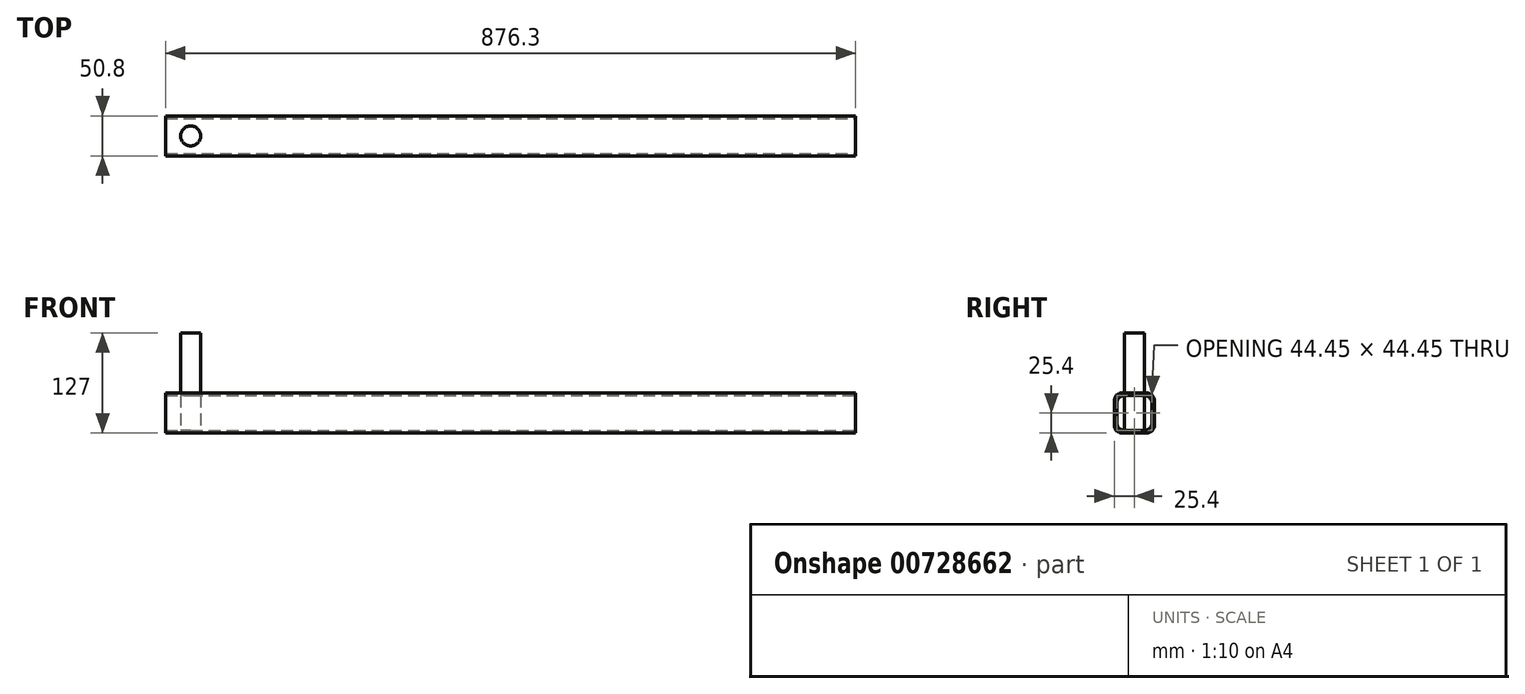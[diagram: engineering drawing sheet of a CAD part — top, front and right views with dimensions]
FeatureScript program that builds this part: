
annotation { "Feature Type Name" : "Feature", "Feature Type Description" : "" }
export const myFeature = defineFeature(function(context is Context, id is Id, definition is map)
    precondition{}
    {
        {
            var Q0;
            Q0=qCreatedBy(makeId("Right.planeOp"),FACE);
            var sketch = newSketch(context, id + "F0", { "sketchPlane" : qUnion([Q0])});
            skLineSegment(sketch, "E0.bottom", {"start": v(0, 0) * mm, "end": v(50.8, 0) * mm});
            skLineSegment(sketch, "E0.top", {"start": v(0, 50.8) * mm, "end": v(50.8, 50.8) * mm});
            skLineSegment(sketch, "E0.left", {"start": v(0, 0) * mm, "end": v(0, 50.8) * mm});
            skLineSegment(sketch, "E0.right", {"start": v(50.8, 0) * mm, "end": v(50.8, 50.8) * mm});
            skSolve(sketch);
        }
        {
            var Q0;
            Q0=qSketchRegion(id+"F0",true);
            extrude(context, id + "F1", {"entities" : qUnion([Q0]), "oppositeDirection" : true, "depth" : 876.3 * mm, "offsetDistance" : 25.4 * mm});
        }
        {
            var Q0;
            Q0=makeQuery(id+"F1.opExtrude","CAP_FACE",FACE,{"disambiguationData":[OSD([sQuery(id+"F0.wireOp",EDGE,"E0.bottom"),sQuery(id+"F0.wireOp",EDGE,"E0.top"),sQuery(id+"F0.wireOp",EDGE,"E0.left"),sQuery(id+"F0.wireOp",EDGE,"E0.right")])],"isStart":true});
            var sketch = newSketch(context, id + "F2", { "sketchPlane" : qUnion([Q0])});
            skLineSegment(sketch, "E1.0", {"start": v(3.17, 47.63) * mm, "end": v(47.63, 47.63) * mm});
            skLineSegment(sketch, "E1.1", {"start": v(3.17, 3.17) * mm, "end": v(3.17, 47.63) * mm});
            skLineSegment(sketch, "E1.2", {"start": v(3.17, 3.17) * mm, "end": v(47.63, 3.17) * mm});
            skLineSegment(sketch, "E1.3", {"start": v(47.63, 3.17) * mm, "end": v(47.63, 47.63) * mm});
            skSolve(sketch);
        }
        {
            var Q0;
            Q0=qSketchRegion(id+"F2",true);
            extrude(context, id + "F3", {"entities" : qUnion([Q0]), "operationType" : NewBodyOperationType.REMOVE, "oppositeDirection" : true, "depth" : 876.3 * mm, "offsetDistance" : 25.4 * mm});
        }
        {
            var Q0;
            Q0=makeQuery(id+"F3.boolean.opBoolean","COPY",EDGE,{"derivedFrom":makeQuery(id+"F3.opExtrude","SWEPT_EDGE",EDGE,{"disambiguationData":[OSD([sQuery(id+"F2.wireOp",EDGE,"E1.1"),sQuery(id+"F2.wireOp",EDGE,"E1.2")])]})});
            var Q1;
            Q1=makeQuery(id+"F3.boolean.opBoolean","COPY",EDGE,{"derivedFrom":makeQuery(id+"F3.opExtrude","SWEPT_EDGE",EDGE,{"disambiguationData":[OSD([sQuery(id+"F2.wireOp",EDGE,"E1.2"),sQuery(id+"F2.wireOp",EDGE,"E1.3")])]})});
            var Q2;
            Q2=makeQuery(id+"F3.boolean.opBoolean","COPY",EDGE,{"derivedFrom":makeQuery(id+"F3.opExtrude","SWEPT_EDGE",EDGE,{"disambiguationData":[OSD([sQuery(id+"F2.wireOp",EDGE,"E1.0"),sQuery(id+"F2.wireOp",EDGE,"E1.3")])]})});
            var Q3;
            Q3=makeQuery(id+"F3.boolean.opBoolean","COPY",EDGE,{"derivedFrom":makeQuery(id+"F3.opExtrude","SWEPT_EDGE",EDGE,{"disambiguationData":[OSD([sQuery(id+"F2.wireOp",EDGE,"E1.0"),sQuery(id+"F2.wireOp",EDGE,"E1.1")])]})});
            var Q4;
            Q4=makeQuery(id+"F1.opExtrude","SWEPT_EDGE",EDGE,{"disambiguationData":[OSD([sQuery(id+"F0.wireOp",EDGE,"E0.bottom"),sQuery(id+"F0.wireOp",EDGE,"E0.right")])]});
            var Q5;
            Q5=makeQuery(id+"F1.opExtrude","SWEPT_EDGE",EDGE,{"disambiguationData":[OSD([sQuery(id+"F0.wireOp",EDGE,"E0.top"),sQuery(id+"F0.wireOp",EDGE,"E0.right")])]});
            var Q6;
            Q6=makeQuery(id+"F1.opExtrude","SWEPT_EDGE",EDGE,{"disambiguationData":[OSD([sQuery(id+"F0.wireOp",EDGE,"E0.top"),sQuery(id+"F0.wireOp",EDGE,"E0.left")])]});
            var Q7;
            Q7=makeQuery(id+"F1.opExtrude","SWEPT_EDGE",EDGE,{"disambiguationData":[OSD([sQuery(id+"F0.wireOp",EDGE,"E0.bottom"),sQuery(id+"F0.wireOp",EDGE,"E0.left")])]});
            fillet(context, id + "F4", {"entities" : qUnion([Q0, Q1, Q2, Q3, Q4, Q5, Q6, Q7]), "radius" : 9.52 * mm, "tangentPropagation" : true, "allowEdgeOverflow" : false});
        }
        {
            var Q0;
            Q0=makeQuery(id+"F1.opExtrude","SWEPT_FACE",FACE,{"disambiguationData":[OSD([sQuery(id+"F0.wireOp",EDGE,"E0.top")])]});
            var sketch = newSketch(context, id + "F5", { "sketchPlane" : qUnion([Q0])});
            skLineSegment(sketch, "E2", {"start": v(0, 25.4) * mm, "end": v(-876.3, 25.4) * mm, "construction": true});
            skCircle(sketch, "E3", {"center": v(-844.55, 25.4) * mm, "radius": 12.7 * mm});
            skSolve(sketch);
        }
        {
            var Q0;
            Q0=makeQuery(id+"F5.imprint","IMPRINT",FACE,{"disambiguationData":[TD([[makeQuery(id+"F5.imprint","IMPRINT",EDGE,{"derivedFrom":sQuery(id+"F5.wireOp",EDGE,"E3")}),1.0]])]});
            extrude(context, id + "F6", {"entities" : qUnion([Q0]), "operationType" : NewBodyOperationType.REMOVE, "oppositeDirection" : true, "depth" : 50.8 * mm, "offsetDistance" : 25.4 * mm});
        }
        {
            var Q0;
            Q0=makeQuery(id+"F1.opExtrude","SWEPT_FACE",FACE,{"disambiguationData":[OSD([sQuery(id+"F0.wireOp",EDGE,"E0.bottom")])]});
            var sketch = newSketch(context, id + "F7", { "sketchPlane" : qUnion([Q0])});
            skCircle(sketch, "E4", {"center": v(-844.55, -25.4) * mm, "radius": 12.7 * mm});
            skSolve(sketch);
        }
        {
            var Q0;
            Q0=makeQuery(id+"F7.imprint","IMPRINT",FACE,{"disambiguationData":[TD([[makeQuery(id+"F7.imprint","IMPRINT",EDGE,{"derivedFrom":sQuery(id+"F7.wireOp",EDGE,"E4")}),-1.0]])]});
            extrude(context, id + "F8", {"entities" : qUnion([Q0]), "operationType" : NewBodyOperationType.ADD, "oppositeDirection" : true, "depth" : 127 * mm, "offsetDistance" : 25.4 * mm});
        }
    });
